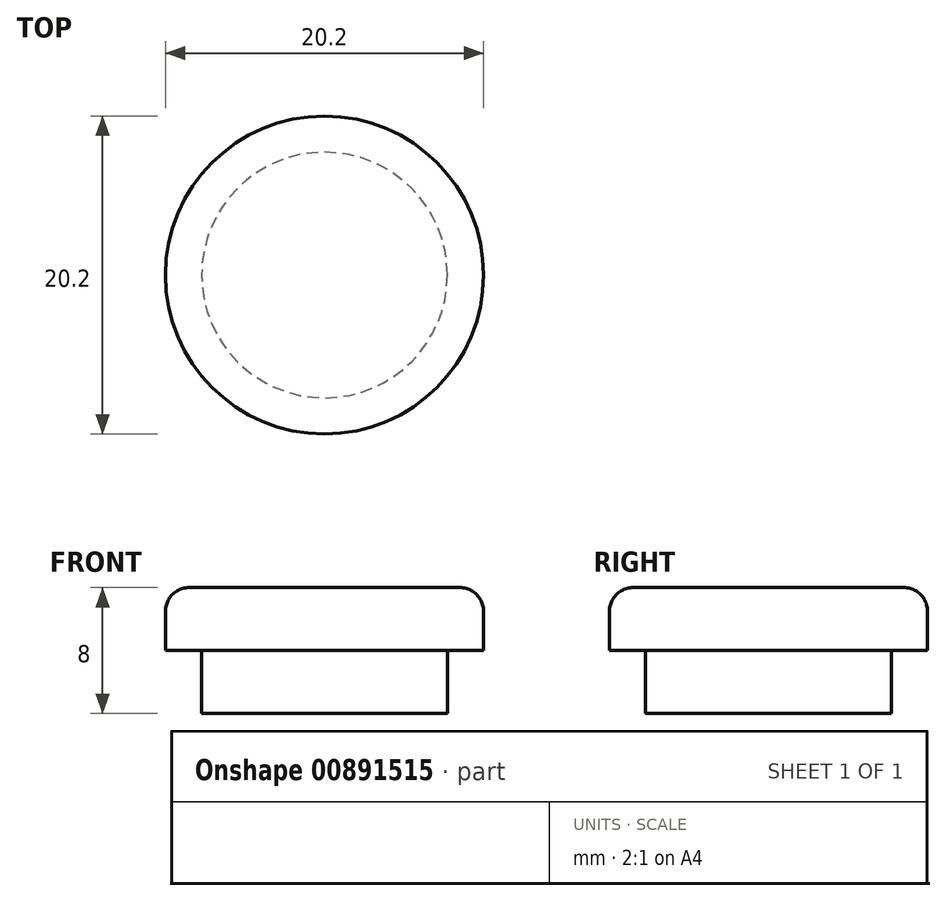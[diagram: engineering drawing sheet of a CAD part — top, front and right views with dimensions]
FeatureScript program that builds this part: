
annotation { "Feature Type Name" : "Feature", "Feature Type Description" : "" }
export const myFeature = defineFeature(function(context is Context, id is Id, definition is map)
    precondition{}
    {
        {
            var Q0;
            Q0=qCreatedBy(makeId("Top.planeOp"),FACE);
            var sketch = newSketch(context, id + "F0", { "sketchPlane" : qUnion([Q0])});
            skCircle(sketch, "E0", {"center": v(0, 0) * mm, "radius": 10.1 * mm});
            skSolve(sketch);
        }
        {
            var Q0;
            Q0 = qSketchRegion(id + "F0", true);
            extrude(context, id + "F1", {"entities" : qUnion([Q0]), "depth" : 4 * mm, "offsetDistance" : 25.4 * mm});
        }
        {
            var Q0;
            Q0=makeQuery(id+"F1.opExtrude","CAP_FACE",FACE,{"disambiguationData":[OSD([sQuery(id+"F0.wireOp",EDGE,"E0")])],"isStart":false});
            fillet(context, id + "F2", {"entities" : qUnion([Q0]), "radius" : 1.5 * mm, "tangentPropagation" : true, "allowEdgeOverflow" : false});
        }
        {
            var Q0;
            Q0=makeQuery(id+"F1.opExtrude","CAP_FACE",FACE,{"disambiguationData":[OSD([sQuery(id+"F0.wireOp",EDGE,"E0")])],"isStart":true});
            var sketch = newSketch(context, id + "F3", { "sketchPlane" : qUnion([Q0])});
            skCircle(sketch, "E1", {"center": v(0, 0) * mm, "radius": 7.8 * mm});
            skSolve(sketch);
        }
        {
            var Q0;
            Q0=makeQuery(id+"F3.imprint","IMPRINT",FACE,{"disambiguationData":[TD([[makeQuery(id+"F3.imprint","IMPRINT",EDGE,{"derivedFrom":sQuery(id+"F3.wireOp",EDGE,"E1")}),1.0]])]});
            extrude(context, id + "F4", {"entities" : qUnion([Q0]), "operationType" : NewBodyOperationType.ADD, "depth" : 4 * mm, "offsetDistance" : 25.4 * mm});
        }
    });
